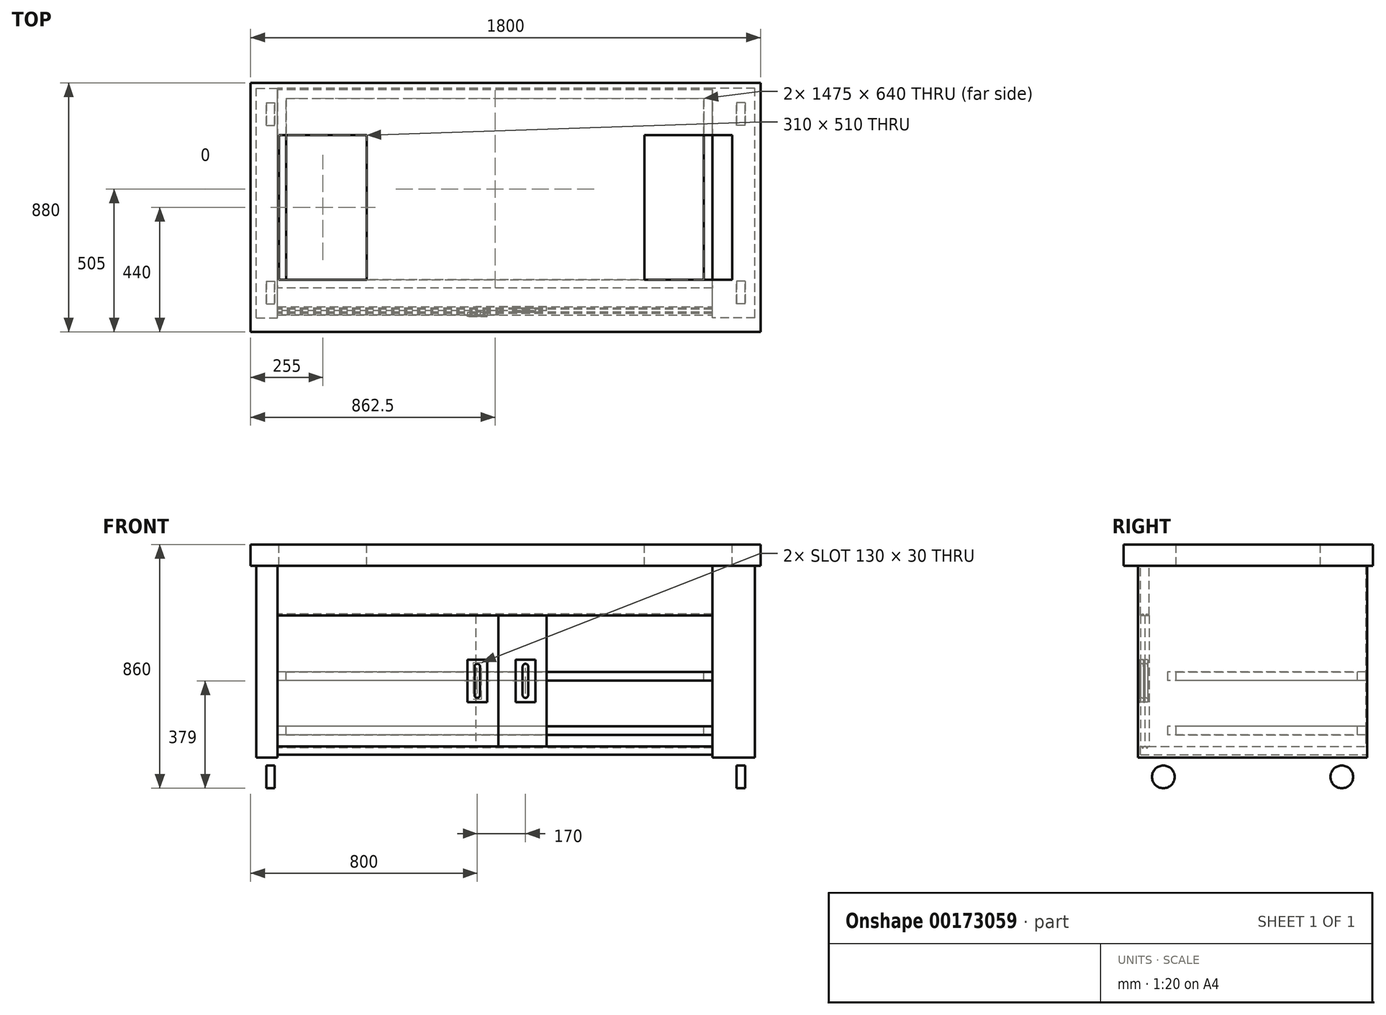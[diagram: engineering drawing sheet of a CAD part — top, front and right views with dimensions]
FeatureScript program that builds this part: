
annotation { "Feature Type Name" : "Feature", "Feature Type Description" : "" }
export const myFeature = defineFeature(function(context is Context, id is Id, definition is map)
    precondition{}
    {
        {
            var Q0;
            Q0=qCreatedBy(makeId("Top.planeOp"),FACE);
            var sketch = newSketch(context, id + "F0", { "sketchPlane" : qUnion([Q0])});
            skLineSegment(sketch, "E0.bottom", {"start": v(900, 440) * mm, "end": v(-900, 440) * mm});
            skLineSegment(sketch, "E0.top", {"start": v(900, -440) * mm, "end": v(-900, -440) * mm});
            skLineSegment(sketch, "E0.left", {"start": v(900, 440) * mm, "end": v(900, -440) * mm});
            skLineSegment(sketch, "E0.right", {"start": v(-900, 440) * mm, "end": v(-900, -440) * mm});
            skPoint(sketch, "E0.middle", {"position": v(0, 0) * mm});
            skSolve(sketch);
        }
        {
            var Q0;
            Q0 = qSketchRegion(id + "F0", true);
            extrude(context, id + "F1", {"entities" : qUnion([Q0]), "depth" : 75 * mm});
        }
        {
            var Q0;
            Q0=makeQuery(id+"F1.opExtrude","CAP_FACE",FACE,{"disambiguationData":[OSD([sQuery(id+"F0.wireOp",EDGE,"E0.bottom"),sQuery(id+"F0.wireOp",EDGE,"E0.top"),sQuery(id+"F0.wireOp",EDGE,"E0.left"),sQuery(id+"F0.wireOp",EDGE,"E0.right")])],"isStart":false});
            var sketch = newSketch(context, id + "F2", { "sketchPlane" : qUnion([Q0])});
            skLineSegment(sketch, "E1.bottom", {"start": v(-800, 255) * mm, "end": v(-490, 255) * mm});
            skLineSegment(sketch, "E1.top", {"start": v(-800, -255) * mm, "end": v(-490, -255) * mm});
            skLineSegment(sketch, "E1.left", {"start": v(-800, 255) * mm, "end": v(-800, -255) * mm});
            skLineSegment(sketch, "E1.right", {"start": v(-490, 255) * mm, "end": v(-490, -255) * mm});
            skLineSegment(sketch, "E2.bottom", {"start": v(490, 255) * mm, "end": v(800, 255) * mm});
            skLineSegment(sketch, "E2.top", {"start": v(490, -255) * mm, "end": v(800, -255) * mm});
            skLineSegment(sketch, "E2.left", {"start": v(490, 255) * mm, "end": v(490, -255) * mm});
            skLineSegment(sketch, "E2.right", {"start": v(800, 255) * mm, "end": v(800, -255) * mm});
            skSolve(sketch);
        }
        {
            var Q0;
            Q0 = qSketchRegion(id + "F2", true);
            extrude(context, id + "F3", {"entities" : qUnion([Q0]), "operationType" : NewBodyOperationType.REMOVE, "endBound" : BoundingType.THROUGH_ALL, "oppositeDirection" : true, "depth" : 50 * mm});
        }
        {
            var Q0;
            Q0=makeQuery(id+"F1.opExtrude","CAP_FACE",FACE,{"disambiguationData":[OSD([sQuery(id+"F0.wireOp",EDGE,"E0.bottom"),sQuery(id+"F0.wireOp",EDGE,"E0.top"),sQuery(id+"F0.wireOp",EDGE,"E0.left"),sQuery(id+"F0.wireOp",EDGE,"E0.right")])],"isStart":true});
            var sketch = newSketch(context, id + "F4", { "sketchPlane" : qUnion([Q0])});
            skLineSegment(sketch, "E3.bottom", {"start": v(-880, 390) * mm, "end": v(-805, 390) * mm});
            skLineSegment(sketch, "E3.top", {"start": v(-880, -420) * mm, "end": v(-805, -420) * mm});
            skLineSegment(sketch, "E3.left", {"start": v(-880, 390) * mm, "end": v(-880, -420) * mm});
            skLineSegment(sketch, "E3.right", {"start": v(-805, 390) * mm, "end": v(-805, -420) * mm});
            skLineSegment(sketch, "E4.bottom", {"start": v(880, 390) * mm, "end": v(730, 390) * mm});
            skLineSegment(sketch, "E4.top", {"start": v(880, -420) * mm, "end": v(730, -420) * mm});
            skLineSegment(sketch, "E4.left", {"start": v(880, 390) * mm, "end": v(880, -420) * mm});
            skLineSegment(sketch, "E4.right", {"start": v(730, 390) * mm, "end": v(730, -420) * mm});
            skSolve(sketch);
        }
        {
            var Q0;
            Q0 = qSketchRegion(id + "F4", true);
            extrude(context, id + "F5", {"entities" : qUnion([Q0]), "operationType" : NewBodyOperationType.ADD, "depth" : 677 * mm});
        }
        {
            var Q0;
            Q0=makeQuery(id+"F5.opExtrude","SWEPT_FACE",FACE,{"disambiguationData":[OSD([sQuery(id+"F4.wireOp",EDGE,"E4.right")])]});
            var sketch = newSketch(context, id + "F6", { "sketchPlane" : qUnion([Q0])});
            skLineSegment(sketch, "E5.bottom", {"start": v(380, 0) * mm, "end": v(350, 0) * mm});
            skLineSegment(sketch, "E5.top", {"start": v(380, -175) * mm, "end": v(350, -175) * mm});
            skLineSegment(sketch, "E5.left", {"start": v(380, 0) * mm, "end": v(380, -175) * mm});
            skLineSegment(sketch, "E5.right", {"start": v(350, 0) * mm, "end": v(350, -175) * mm});
            skSolve(sketch);
        }
        {
            var Q0;
            Q0 = qSketchRegion(id + "F6", true);
            extrude(context, id + "F7", {"entities" : qUnion([Q0]), "operationType" : NewBodyOperationType.ADD, "endBound" : BoundingType.UP_TO_NEXT, "depth" : 25 * mm});
        }
        {
            var Q0;
            Q0=makeQuery(id+"F5.opExtrude","SWEPT_FACE",FACE,{"disambiguationData":[OSD([sQuery(id+"F4.wireOp",EDGE,"E3.right")])]});
            var sketch = newSketch(context, id + "F8", { "sketchPlane" : qUnion([Q0])});
            skLineSegment(sketch, "E6.bottom", {"start": v(-380, -667) * mm, "end": v(420, -667) * mm});
            skLineSegment(sketch, "E6.top", {"start": v(-380, -637) * mm, "end": v(420, -637) * mm});
            skLineSegment(sketch, "E6.left", {"start": v(-380, -667) * mm, "end": v(-380, -637) * mm});
            skLineSegment(sketch, "E6.right", {"start": v(420, -667) * mm, "end": v(420, -637) * mm});
            skSolve(sketch);
        }
        {
            var Q0;
            Q0 = qSketchRegion(id + "F8", true);
            extrude(context, id + "F9", {"entities" : qUnion([Q0]), "endBound" : BoundingType.UP_TO_NEXT, "depth" : 25 * mm});
        }
        {
            var Q0;
            Q0=makeQuery(id+"F9.opExtrude","SWEPT_FACE",FACE,{"disambiguationData":[OSD([sQuery(id+"F8.wireOp",EDGE,"E6.top")])]});
            var sketch = newSketch(context, id + "F10", { "sketchPlane" : qUnion([Q0])});
            skLineSegment(sketch, "E7.bottom", {"start": v(730, 420) * mm, "end": v(-805, 420) * mm});
            skLineSegment(sketch, "E7.top", {"start": v(730, 415) * mm, "end": v(-805, 415) * mm});
            skLineSegment(sketch, "E7.left", {"start": v(730, 420) * mm, "end": v(730, 415) * mm});
            skLineSegment(sketch, "E7.right", {"start": v(-805, 420) * mm, "end": v(-805, 415) * mm});
            skSolve(sketch);
        }
        {
            var Q0;
            Q0 = qSketchRegion(id + "F10", true);
            extrude(context, id + "F11", {"entities" : qUnion([Q0]), "endBound" : BoundingType.UP_TO_NEXT, "depth" : 25 * mm});
        }
        {
            var Q0;
            Q0=makeQuery(id+"F5.opExtrude","SWEPT_FACE",FACE,{"disambiguationData":[OSD([sQuery(id+"F4.wireOp",EDGE,"E3.right")])]});
            var sketch = newSketch(context, id + "F12", { "sketchPlane" : qUnion([Q0])});
            skLineSegment(sketch, "E8.bottom", {"start": v(415, -375) * mm, "end": v(-285, -375) * mm});
            skLineSegment(sketch, "E8.top", {"start": v(415, -405) * mm, "end": v(-285, -405) * mm});
            skLineSegment(sketch, "E8.left", {"start": v(415, -375) * mm, "end": v(415, -405) * mm});
            skLineSegment(sketch, "E8.right", {"start": v(-285, -375) * mm, "end": v(-285, -405) * mm});
            skLineSegment(sketch, "E9.bottom", {"start": v(415, -567) * mm, "end": v(-285, -567) * mm});
            skLineSegment(sketch, "E9.top", {"start": v(415, -597) * mm, "end": v(-285, -597) * mm});
            skLineSegment(sketch, "E9.left", {"start": v(415, -567) * mm, "end": v(415, -597) * mm});
            skLineSegment(sketch, "E9.right", {"start": v(-285, -567) * mm, "end": v(-285, -597) * mm});
            skSolve(sketch);
        }
        {
            var Q0;
            Q0 = qSketchRegion(id + "F12", true);
            extrude(context, id + "F13", {"entities" : qUnion([Q0]), "endBound" : BoundingType.UP_TO_NEXT, "depth" : 25 * mm});
        }
        {
            var Q0;
            Q0=makeQuery(id+"F13.opExtrude","SWEPT_FACE",FACE,{"disambiguationData":[OSD([sQuery(id+"F12.wireOp",EDGE,"E8.bottom")])]});
            var sketch = newSketch(context, id + "F14", { "sketchPlane" : qUnion([Q0])});
            skLineSegment(sketch, "E10.bottom", {"start": v(-775, -255) * mm, "end": v(700, -255) * mm});
            skLineSegment(sketch, "E10.top", {"start": v(-775, 385) * mm, "end": v(700, 385) * mm});
            skLineSegment(sketch, "E10.left", {"start": v(-775, -255) * mm, "end": v(-775, 385) * mm});
            skLineSegment(sketch, "E10.right", {"start": v(700, -255) * mm, "end": v(700, 385) * mm});
            skSolve(sketch);
        }
        {
            var Q0;
            Q0 = qSketchRegion(id + "F14", true);
            var Q1;
            Q1=makeQuery(id+"F13.opExtrude","SWEPT_FACE",FACE,{"disambiguationData":[OSD([sQuery(id+"F12.wireOp",EDGE,"E9.top")])]});
            extrude(context, id + "F15", {"entities" : qUnion([Q0]), "operationType" : NewBodyOperationType.REMOVE, "endBound" : BoundingType.UP_TO_SURFACE, "oppositeDirection" : true, "endBoundEntityFace" : qUnion([Q1]), "depth" : 250 * mm});
        }
        {
            var Q0;
            Q0=makeQuery(id+"F5.opExtrude","SWEPT_FACE",FACE,{"disambiguationData":[OSD([sQuery(id+"F4.wireOp",EDGE,"E3.right")])]});
            var sketch = newSketch(context, id + "F16", { "sketchPlane" : qUnion([Q0])});
            skLineSegment(sketch, "E11", {"start": v(-375, -175) * mm, "end": v(-375, -170) * mm});
            skLineSegment(sketch, "E12", {"start": v(-375, -170) * mm, "end": v(-370, -170) * mm});
            skLineSegment(sketch, "E13", {"start": v(-370, -170) * mm, "end": v(-370, -175) * mm});
            skLineSegment(sketch, "E14", {"start": v(-375, -637) * mm, "end": v(-375, -642) * mm});
            skLineSegment(sketch, "E15", {"start": v(-375, -642) * mm, "end": v(-370, -642) * mm});
            skLineSegment(sketch, "E16", {"start": v(-370, -642) * mm, "end": v(-370, -637) * mm});
            skLineSegment(sketch, "E17", {"start": v(-360, -175) * mm, "end": v(-360, -170) * mm});
            skLineSegment(sketch, "E18", {"start": v(-360, -170) * mm, "end": v(-355, -170) * mm});
            skLineSegment(sketch, "E19", {"start": v(-355, -170) * mm, "end": v(-355, -175) * mm});
            skLineSegment(sketch, "E20", {"start": v(-360, -637) * mm, "end": v(-360, -642) * mm});
            skLineSegment(sketch, "E21", {"start": v(-360, -642) * mm, "end": v(-355, -642) * mm});
            skLineSegment(sketch, "E22", {"start": v(-355, -642) * mm, "end": v(-355, -637) * mm});
            skLineSegment(sketch, "E23", {"start": v(-375, -175) * mm, "end": v(-370, -175) * mm});
            skLineSegment(sketch, "E24", {"start": v(-360, -175) * mm, "end": v(-355, -175) * mm});
            skLineSegment(sketch, "E25", {"start": v(-375, -637) * mm, "end": v(-370, -637) * mm});
            skLineSegment(sketch, "E26", {"start": v(-360, -637) * mm, "end": v(-355, -637) * mm});
            skSolve(sketch);
        }
        {
            var Q0;
            Q0 = qSketchRegion(id + "F16", true);
            var Q1;
            Q1=makeQuery(id+"F5.opExtrude","SWEPT_FACE",FACE,{"disambiguationData":[OSD([sQuery(id+"F4.wireOp",EDGE,"E4.right")])]});
            extrude(context, id + "F17", {"entities" : qUnion([Q0]), "operationType" : NewBodyOperationType.REMOVE, "endBound" : BoundingType.UP_TO_SURFACE, "endBoundEntityFace" : qUnion([Q1]), "depth" : 25 * mm});
        }
        {
            var Q0;
            Q0=makeQuery(id+"F17.boolean.opBoolean","MERGE",FACE,{"derivedFrom":[makeQuery(id+"F5.opExtrude","SWEPT_FACE",FACE,{"disambiguationData":[OSD([sQuery(id+"F4.wireOp",EDGE,"E3.right")])]}),makeQuery(id+"F17.opExtrude","CAP_FACE",FACE,{"disambiguationData":[OSD([sQuery(id+"F16.wireOp",EDGE,"E11"),sQuery(id+"F16.wireOp",EDGE,"E12"),sQuery(id+"F16.wireOp",EDGE,"E13"),sQuery(id+"F16.wireOp",EDGE,"E23")])],"isStart":true}),makeQuery(id+"F17.opExtrude","CAP_FACE",FACE,{"disambiguationData":[OSD([sQuery(id+"F16.wireOp",EDGE,"E17"),sQuery(id+"F16.wireOp",EDGE,"E18"),sQuery(id+"F16.wireOp",EDGE,"E19"),sQuery(id+"F16.wireOp",EDGE,"E24")])],"isStart":true})]});
            var sketch = newSketch(context, id + "F18", { "sketchPlane" : qUnion([Q0])});
            skLineSegment(sketch, "E27.bottom", {"start": v(-380, -175) * mm, "end": v(-365, -175) * mm});
            skLineSegment(sketch, "E27.top", {"start": v(-380, -637) * mm, "end": v(-365, -637) * mm});
            skLineSegment(sketch, "E27.left", {"start": v(-380, -175) * mm, "end": v(-380, -637) * mm});
            skLineSegment(sketch, "E27.right", {"start": v(-365, -175) * mm, "end": v(-365, -637) * mm});
            skSolve(sketch);
        }
        {
            var Q0;
            Q0 = qSketchRegion(id + "F18", true);
            extrude(context, id + "F19", {"entities" : qUnion([Q0]), "depth" : 780 * mm});
        }
        {
            var Q0;
            Q0=makeQuery(id+"F17.boolean.opBoolean","MERGE",FACE,{"derivedFrom":[makeQuery(id+"F5.opExtrude","SWEPT_FACE",FACE,{"disambiguationData":[OSD([sQuery(id+"F4.wireOp",EDGE,"E3.right")])]}),makeQuery(id+"F17.opExtrude","CAP_FACE",FACE,{"disambiguationData":[OSD([sQuery(id+"F16.wireOp",EDGE,"E11"),sQuery(id+"F16.wireOp",EDGE,"E12"),sQuery(id+"F16.wireOp",EDGE,"E13"),sQuery(id+"F16.wireOp",EDGE,"E23")])],"isStart":true}),makeQuery(id+"F17.opExtrude","CAP_FACE",FACE,{"disambiguationData":[OSD([sQuery(id+"F16.wireOp",EDGE,"E17"),sQuery(id+"F16.wireOp",EDGE,"E18"),sQuery(id+"F16.wireOp",EDGE,"E19"),sQuery(id+"F16.wireOp",EDGE,"E24")])],"isStart":true})]});
            cPlane(context, id + "F20", {"entities" : qUnion([Q0]), "cplaneType" : CPlaneType.OFFSET, "offset" : 700 * mm, "width" : 150 * mm, "height" : 150 * mm});
        }
        {
            var Q0;
            Q0=qCreatedBy(id+"F20.planeOp",FACE);
            var sketch = newSketch(context, id + "F21", { "sketchPlane" : qUnion([Q0])});
            skLineSegment(sketch, "E28.bottom", {"start": v(-365, -175) * mm, "end": v(-350, -175) * mm});
            skLineSegment(sketch, "E28.top", {"start": v(-365, -637) * mm, "end": v(-350, -637) * mm});
            skLineSegment(sketch, "E28.left", {"start": v(-365, -175) * mm, "end": v(-365, -637) * mm});
            skLineSegment(sketch, "E28.right", {"start": v(-350, -175) * mm, "end": v(-350, -637) * mm});
            skSolve(sketch);
        }
        {
            var Q0;
            Q0 = qSketchRegion(id + "F21", true);
            extrude(context, id + "F22", {"entities" : qUnion([Q0]), "depth" : 250 * mm});
        }
        {
            var Q0;
            Q0=makeQuery(id+"F19.opExtrude","SWEPT_FACE",FACE,{"disambiguationData":[OSD([sQuery(id+"F18.wireOp",EDGE,"E27.left")])]});
            var sketch = newSketch(context, id + "F23", { "sketchPlane" : qUnion([Q0])});
            skLineSegment(sketch, "E29", {"start": v(-100, -356) * mm, "end": v(-100, -456) * mm});
            skArc(sketch, "E30.0.startCap", {"start": v(-110, -356) * mm, "mid": v(-100, -346) * mm, "end": v(-90, -356) * mm});
            skArc(sketch, "E30.0.endCap", {"start": v(-90, -456) * mm, "mid": v(-100, -466) * mm, "end": v(-110, -456) * mm});
            skLineSegment(sketch, "E30.0.left", {"start": v(-90, -356) * mm, "end": v(-90, -456) * mm});
            skLineSegment(sketch, "E30.0.right", {"start": v(-110, -356) * mm, "end": v(-110, -456) * mm});
            skLineSegment(sketch, "E31.bottom", {"start": v(-135, -331) * mm, "end": v(-65, -331) * mm});
            skLineSegment(sketch, "E31.top", {"start": v(-135, -481) * mm, "end": v(-65, -481) * mm});
            skLineSegment(sketch, "E31.left", {"start": v(-135, -331) * mm, "end": v(-135, -481) * mm});
            skLineSegment(sketch, "E31.right", {"start": v(-65, -331) * mm, "end": v(-65, -481) * mm});
            skSolve(sketch);
        }
        {
            var Q0;
            Q0 = qSketchRegion(id + "F23", true);
            extrude(context, id + "F24", {"entities" : qUnion([Q0]), "depth" : 5 * mm});
        }
        {
            var Q0;
            Q0=makeQuery(id+"F24.opExtrude","SWEPT_EDGE",EDGE,{"disambiguationData":[OSD([sQuery(id+"F23.wireOp",EDGE,"E31.bottom"),sQuery(id+"F23.wireOp",EDGE,"E31.left")])]});
            var Q1;
            Q1=makeQuery(id+"F24.opExtrude","SWEPT_EDGE",EDGE,{"disambiguationData":[OSD([sQuery(id+"F23.wireOp",EDGE,"E31.bottom"),sQuery(id+"F23.wireOp",EDGE,"E31.right")])]});
            var Q2;
            Q2=makeQuery(id+"F24.opExtrude","SWEPT_EDGE",EDGE,{"disambiguationData":[OSD([sQuery(id+"F23.wireOp",EDGE,"E31.top"),sQuery(id+"F23.wireOp",EDGE,"E31.left")])]});
            var Q3;
            Q3=makeQuery(id+"F24.opExtrude","SWEPT_EDGE",EDGE,{"disambiguationData":[OSD([sQuery(id+"F23.wireOp",EDGE,"E31.top"),sQuery(id+"F23.wireOp",EDGE,"E31.right")])]});
            fillet(context, id + "F25", {"entities" : qUnion([Q0, Q1, Q2, Q3]), "radius" : 5 * mm, "tangentPropagation" : true, "allowEdgeOverflow" : false});
        }
        {
            var Q0;
            Q0=makeQuery(id+"F23.imprint","IMPRINT",FACE,{"disambiguationData":[TD([[makeQuery(id+"F23.imprint","IMPRINT",EDGE,{"derivedFrom":sQuery(id+"F23.wireOp",EDGE,"E30.0.startCap")}),-1.0]])]});
            extrude(context, id + "F26", {"entities" : qUnion([Q0]), "operationType" : NewBodyOperationType.REMOVE, "oppositeDirection" : true, "depth" : 10 * mm});
        }
        {
            var Q0;
            Q0=makeQuery(id+"F26.boolean.opBoolean","COPY",EDGE,{"derivedFrom":makeQuery(id+"F26.opExtrude","CAP_EDGE",EDGE,{"disambiguationData":[OSD([sQuery(id+"F23.wireOp",EDGE,"E30.0.right")])],"isStart":false})});
            fillet(context, id + "F27", {"entities" : qUnion([Q0]), "radius" : 5 * mm, "tangentPropagation" : true, "allowEdgeOverflow" : false});
        }
        {
            var Q0;
            Q0=makeQuery(id+"F22.opExtrude","SWEPT_FACE",FACE,{"disambiguationData":[OSD([sQuery(id+"F21.wireOp",EDGE,"E28.left")])]});
            var sketch = newSketch(context, id + "F28", { "sketchPlane" : qUnion([Q0])});
            skLineSegment(sketch, "E32.bottom", {"start": v(35, -331) * mm, "end": v(105, -331) * mm});
            skLineSegment(sketch, "E32.top", {"start": v(35, -481) * mm, "end": v(105, -481) * mm});
            skLineSegment(sketch, "E32.left", {"start": v(35, -331) * mm, "end": v(35, -481) * mm});
            skLineSegment(sketch, "E32.right", {"start": v(105, -331) * mm, "end": v(105, -481) * mm});
            skLineSegment(sketch, "E33", {"start": v(70, -356) * mm, "end": v(70, -456) * mm});
            skPoint(sketch, "E33.startSnap0", {"position": v(70, -331) * mm});
            skArc(sketch, "E34.0.startCap", {"start": v(60, -356) * mm, "mid": v(70, -346) * mm, "end": v(80, -356) * mm});
            skArc(sketch, "E34.0.endCap", {"start": v(80, -456) * mm, "mid": v(70, -466) * mm, "end": v(60, -456) * mm});
            skLineSegment(sketch, "E34.0.left", {"start": v(80, -356) * mm, "end": v(80, -456) * mm});
            skLineSegment(sketch, "E34.0.right", {"start": v(60, -356) * mm, "end": v(60, -456) * mm});
            skSolve(sketch);
        }
        {
            var Q0;
            Q0=makeQuery(id+"F28.imprint","IMPRINT",FACE,{"disambiguationData":[TD([[makeQuery(id+"F28.imprint","IMPRINT",EDGE,{"derivedFrom":sQuery(id+"F28.wireOp",EDGE,"E32.bottom")}),-1.0]])]});
            extrude(context, id + "F29", {"entities" : qUnion([Q0]), "depth" : 5 * mm});
        }
        {
            var Q0;
            Q0=makeQuery(id+"F29.opExtrude","SWEPT_EDGE",EDGE,{"disambiguationData":[OSD([sQuery(id+"F28.wireOp",EDGE,"E32.bottom"),sQuery(id+"F28.wireOp",EDGE,"E32.left")])]});
            var Q1;
            Q1=makeQuery(id+"F29.opExtrude","SWEPT_EDGE",EDGE,{"disambiguationData":[OSD([sQuery(id+"F28.wireOp",EDGE,"E32.bottom"),sQuery(id+"F28.wireOp",EDGE,"E32.right")])]});
            var Q2;
            Q2=makeQuery(id+"F29.opExtrude","SWEPT_EDGE",EDGE,{"disambiguationData":[OSD([sQuery(id+"F28.wireOp",EDGE,"E32.top"),sQuery(id+"F28.wireOp",EDGE,"E32.left")])]});
            var Q3;
            Q3=makeQuery(id+"F29.opExtrude","SWEPT_EDGE",EDGE,{"disambiguationData":[OSD([sQuery(id+"F28.wireOp",EDGE,"E32.top"),sQuery(id+"F28.wireOp",EDGE,"E32.right")])]});
            fillet(context, id + "F30", {"entities" : qUnion([Q0, Q1, Q2, Q3]), "radius" : 5 * mm, "tangentPropagation" : true, "allowEdgeOverflow" : false});
        }
        {
            var Q0;
            Q0=makeQuery(id+"F28.imprint","IMPRINT",FACE,{"disambiguationData":[TD([[makeQuery(id+"F28.imprint","IMPRINT",EDGE,{"derivedFrom":sQuery(id+"F28.wireOp",EDGE,"E34.0.startCap")}),-1.0]])]});
            extrude(context, id + "F31", {"entities" : qUnion([Q0]), "operationType" : NewBodyOperationType.REMOVE, "oppositeDirection" : true, "depth" : 10 * mm});
        }
        {
            var Q0;
            Q0=makeQuery(id+"F31.boolean.opBoolean","COPY",EDGE,{"derivedFrom":makeQuery(id+"F31.opExtrude","CAP_EDGE",EDGE,{"disambiguationData":[OSD([sQuery(id+"F28.wireOp",EDGE,"E34.0.right")])],"isStart":false})});
            fillet(context, id + "F32", {"entities" : qUnion([Q0]), "radius" : 5 * mm, "tangentPropagation" : true, "allowEdgeOverflow" : false});
        }
        {
            var Q0;
            Q0=makeQuery(id+"F24.opExtrude","CAP_EDGE",EDGE,{"disambiguationData":[OSD([sQuery(id+"F23.wireOp",EDGE,"E30.0.right")])],"isStart":false});
            var Q1;
            Q1=makeQuery(id+"F29.opExtrude","CAP_EDGE",EDGE,{"disambiguationData":[OSD([sQuery(id+"F28.wireOp",EDGE,"E34.0.right")])],"isStart":false});
            fillet(context, id + "F33", {"entities" : qUnion([Q0, Q1]), "radius" : 5 * mm, "tangentPropagation" : true, "allowEdgeOverflow" : false});
        }
        {
            var Q0;
            Q0=makeQuery(id+"F5.opExtrude","SWEPT_FACE",FACE,{"disambiguationData":[OSD([sQuery(id+"F4.wireOp",EDGE,"E4.left")])]});
            cPlane(context, id + "F34", {"entities" : qUnion([Q0]), "cplaneType" : CPlaneType.OFFSET, "offset" : 50 * mm, "oppositeDirection" : true, "width" : 150 * mm, "height" : 150 * mm});
        }
        {
            var Q0;
            Q0=qCreatedBy(id+"F34.planeOp",FACE);
            var sketch = newSketch(context, id + "F35", { "sketchPlane" : qUnion([Q0])});
            skCircle(sketch, "E35", {"center": v(-300, -745) * mm, "radius": 40 * mm});
            skCircle(sketch, "E36", {"center": v(330, -745) * mm, "radius": 40 * mm});
            skSolve(sketch);
        }
        {
            var Q0;
            Q0 = qSketchRegion(id + "F35", true);
            extrude(context, id + "F36", {"entities" : qUnion([Q0]), "depth" : 15 * mm, "hasSecondDirection" : true, "secondDirectionOppositeDirection" : true, "secondDirectionDepth" : 15 * mm});
        }
        {
            var Q0;
            Q0=makeQuery(id+"F5.opExtrude","SWEPT_FACE",FACE,{"disambiguationData":[OSD([sQuery(id+"F4.wireOp",EDGE,"E3.left")])]});
            cPlane(context, id + "F37", {"entities" : qUnion([Q0]), "cplaneType" : CPlaneType.OFFSET, "offset" : 50 * mm, "oppositeDirection" : true, "width" : 150 * mm, "height" : 150 * mm});
        }
        {
            var Q0;
            Q0=qCreatedBy(id+"F37.planeOp",FACE);
            var sketch = newSketch(context, id + "F38", { "sketchPlane" : qUnion([Q0])});
            skCircle(sketch, "E37", {"center": v(-330, -745) * mm, "radius": 40 * mm});
            skCircle(sketch, "E38", {"center": v(300, -745) * mm, "radius": 40 * mm});
            skSolve(sketch);
        }
        {
            var Q0;
            Q0 = qSketchRegion(id + "F38", true);
            extrude(context, id + "F39", {"entities" : qUnion([Q0]), "depth" : 15 * mm, "hasSecondDirection" : true, "secondDirectionOppositeDirection" : true, "secondDirectionDepth" : 15 * mm});
        }
    });
